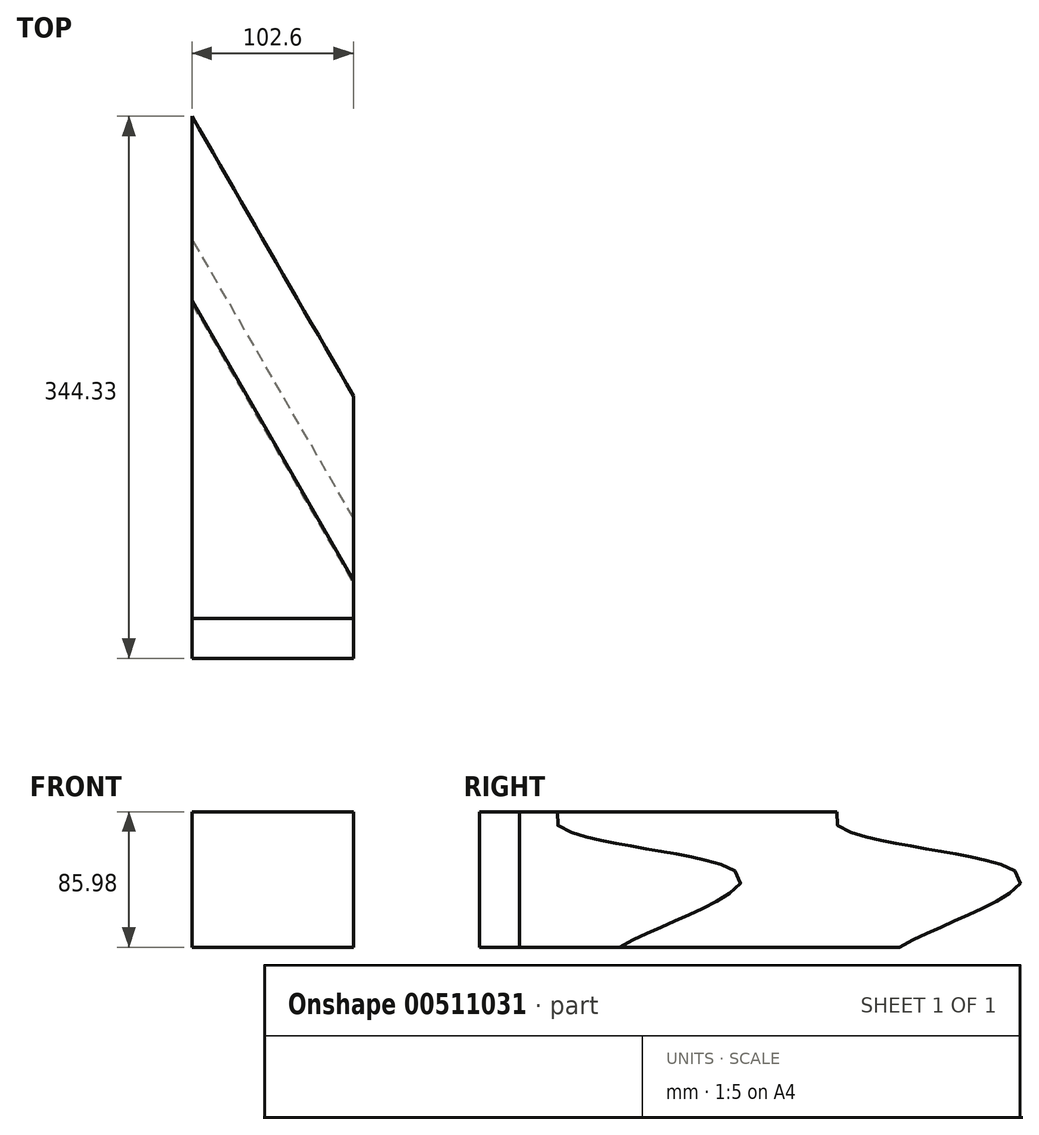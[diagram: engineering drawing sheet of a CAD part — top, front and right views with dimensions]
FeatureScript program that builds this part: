
annotation { "Feature Type Name" : "Feature", "Feature Type Description" : "" }
export const myFeature = defineFeature(function(context is Context, id is Id, definition is map)
    precondition{}
    {
        {
            var Q0;
            Q0=qCreatedBy(makeId("Front.planeOp"),FACE);
            var sketch = newSketch(context, id + "F0", { "sketchPlane" : qUnion([Q0])});
            skLineSegment(sketch, "E0.bottom", {"start": v(-73.23, 46.51) * mm, "end": v(29.37, 46.51) * mm});
            skLineSegment(sketch, "E0.top", {"start": v(-73.23, -39.47) * mm, "end": v(29.37, -39.47) * mm});
            skLineSegment(sketch, "E0.left", {"start": v(-73.23, 46.51) * mm, "end": v(-73.23, -39.47) * mm});
            skLineSegment(sketch, "E0.right", {"start": v(29.37, 46.51) * mm, "end": v(29.37, -39.47) * mm});
            skSolve(sketch);
        }
        {
            var Q0;
            Q0 = qSketchRegion(id + "F0", true);
            extrude(context, id + "F1", {"entities" : qUnion([Q0]), "depth" : 25.4 * mm});
        }
        {
            var Q0;
            Q0=makeQuery(id+"F1.opExtrude","CAP_EDGE",EDGE,{"disambiguationData":[OSD([sQuery(id+"F0.wireOp",EDGE,"E0.right")])],"isStart":false});
            cPlane(context, id + "F2", {"entities" : qUnion([Q0]), "cplaneType" : CPlaneType.LINE_ANGLE, "offset" : 25.4 * mm, "angle" : 60 * degree, "width" : 152.4 * mm, "height" : 152.4 * mm});
        }
        {
            var Q0;
            Q0=qCreatedBy(id+"F2.planeOp",FACE);
            var sketch = newSketch(context, id + "F3", { "sketchPlane" : qUnion([Q0])});
            skFitSpline(sketch, "E1", {"points": [v(-58.27, 70.6) * mm, v(-38.73, 36.23) * mm, v(-95.9, 5.36) * mm, v(-51.75, -47.82) * mm, v(-73.5, -73.2) * mm], "startDerivative": vector(184.12, -172.13) * mm, "endDerivative": vector(-190.98, -106.88) * mm});
            skSolve(sketch);
        }
        {
            var Q0;
            Q0=sQuery(id+"F3.wireOp",EDGE,"E1");
            extrude(context, id + "F4", {"bodyType" : ToolBodyType.SURFACE, "surfaceEntities" : qUnion([Q0]), "depth" : 537.46 * mm});
        }
        {
            var Q0;
            Q0=makeQuery(id+"F1.opExtrude","CAP_FACE",FACE,{"disambiguationData":[OSD([sQuery(id+"F0.wireOp",EDGE,"E0.bottom"),sQuery(id+"F0.wireOp",EDGE,"E0.top"),sQuery(id+"F0.wireOp",EDGE,"E0.left"),sQuery(id+"F0.wireOp",EDGE,"E0.right")])],"isStart":true});
            var Q1;
            Q1=makeQuery(id+"F4.opExtrude","SWEPT_BODY",BODY,{"disambiguationData":[OSD([sQuery(id+"F3.wireOp",EDGE,"E1")])]});
            extrude(context, id + "F5", {"entities" : qUnion([Q0]), "endBound" : BoundingType.UP_TO_BODY, "endBoundEntityBody" : qUnion([Q1]), "depth" : 25.4 * mm});
        }
    });
